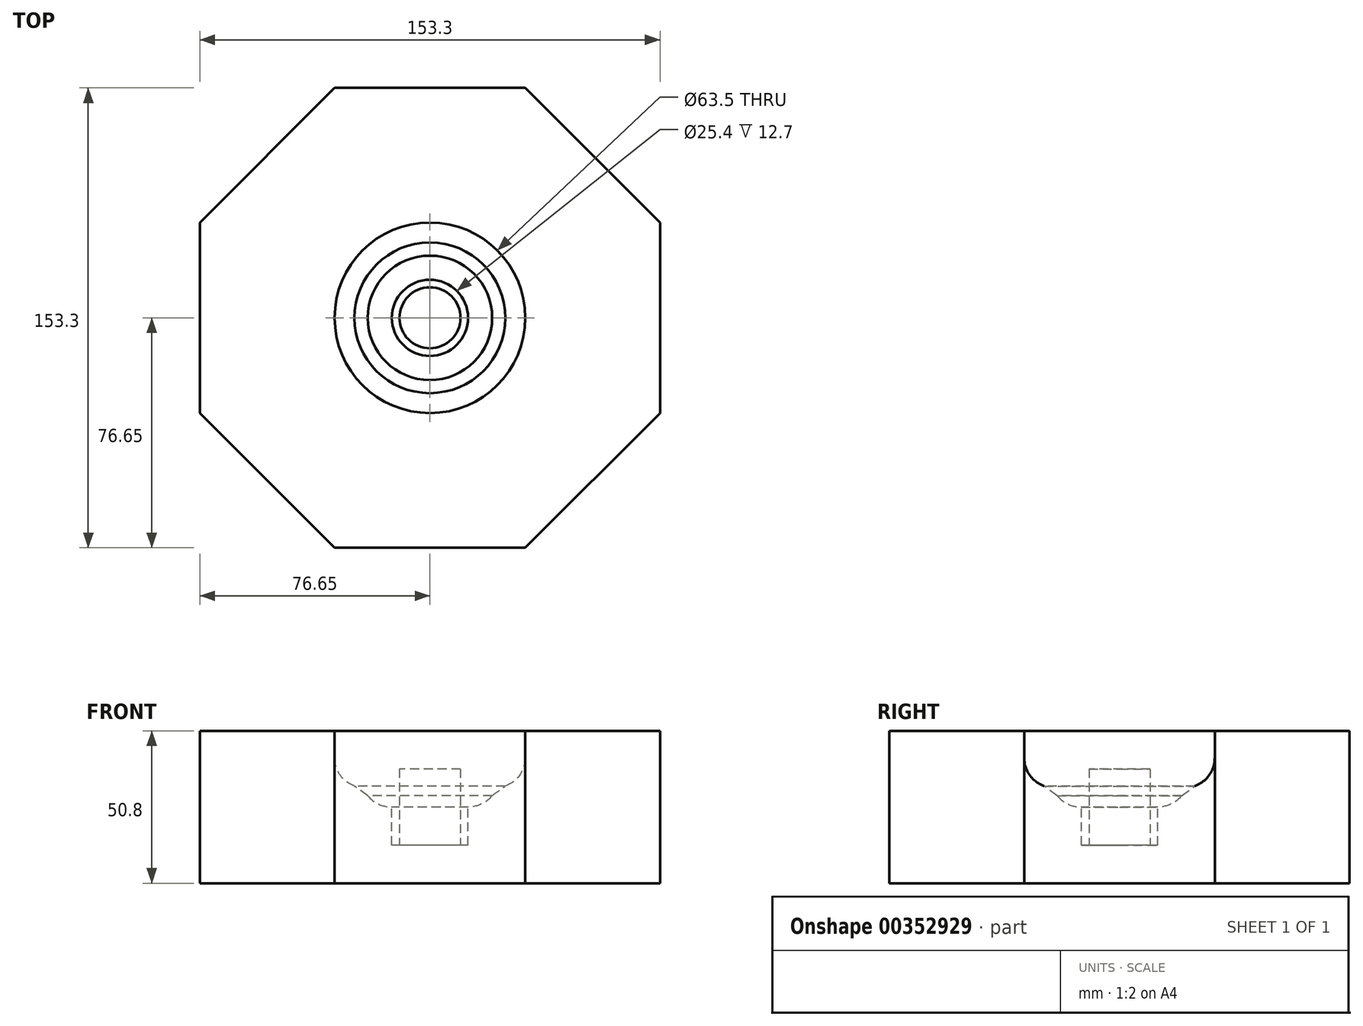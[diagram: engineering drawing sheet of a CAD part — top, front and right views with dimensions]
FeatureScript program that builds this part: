
annotation { "Feature Type Name" : "Feature", "Feature Type Description" : "" }
export const myFeature = defineFeature(function(context is Context, id is Id, definition is map)
    precondition{}
    {
        {
            var Q0;
            Q0=qCreatedBy(makeId("Top.planeOp"),FACE);
            var sketch = newSketch(context, id + "F0", { "sketchPlane" : qUnion([Q0])});
            skCircle(sketch, "E0.cCircle", {"center": v(0, 0) * mm, "radius": 76.65 * mm, "construction": true});
            skLineSegment(sketch, "E0.0", {"start": v(76.65, 31.75) * mm, "end": v(76.65, -31.75) * mm});
            skLineSegment(sketch, "E0.1", {"start": v(76.65, -31.75) * mm, "end": v(31.75, -76.65) * mm});
            skLineSegment(sketch, "E0.2", {"start": v(31.75, -76.65) * mm, "end": v(-31.75, -76.65) * mm});
            skLineSegment(sketch, "E0.3", {"start": v(-31.75, -76.65) * mm, "end": v(-76.65, -31.75) * mm});
            skLineSegment(sketch, "E0.4", {"start": v(-76.65, -31.75) * mm, "end": v(-76.65, 31.75) * mm});
            skLineSegment(sketch, "E0.5", {"start": v(-76.65, 31.75) * mm, "end": v(-31.75, 76.65) * mm});
            skLineSegment(sketch, "E0.6", {"start": v(-31.75, 76.65) * mm, "end": v(31.75, 76.65) * mm});
            skLineSegment(sketch, "E0.7", {"start": v(31.75, 76.65) * mm, "end": v(76.65, 31.75) * mm});
            skPoint(sketch, "E0.0.midPoint", {"position": v(76.65, 0) * mm});
            skSolve(sketch);
        }
        {
            var Q0;
            Q0 = qSketchRegion(id + "F0", true);
            extrude(context, id + "F1", {"entities" : qUnion([Q0]), "depth" : 50.8 * mm});
        }
        {
            var Q0;
            Q0=makeQuery(id+"F1.opExtrude","CAP_FACE",FACE,{"disambiguationData":[OSD([sQuery(id+"F0.wireOp",EDGE,"E0.0"),sQuery(id+"F0.wireOp",EDGE,"E0.1"),sQuery(id+"F0.wireOp",EDGE,"E0.2"),sQuery(id+"F0.wireOp",EDGE,"E0.3"),sQuery(id+"F0.wireOp",EDGE,"E0.4"),sQuery(id+"F0.wireOp",EDGE,"E0.5"),sQuery(id+"F0.wireOp",EDGE,"E0.6"),sQuery(id+"F0.wireOp",EDGE,"E0.7")])],"isStart":false});
            var sketch = newSketch(context, id + "F2", { "sketchPlane" : qUnion([Q0])});
            skCircle(sketch, "E1", {"center": v(0, 0) * mm, "radius": 31.75 * mm});
            skSolve(sketch);
        }
        {
            var Q0;
            Q0 = qSketchRegion(id + "F2", true);
            extrude(context, id + "F3", {"entities" : qUnion([Q0]), "operationType" : NewBodyOperationType.REMOVE, "oppositeDirection" : true, "depth" : 19.05 * mm});
        }
        {
            var Q0;
            Q0=makeQuery(id+"F1.opExtrude","CAP_FACE",FACE,{"disambiguationData":[OSD([sQuery(id+"F0.wireOp",EDGE,"E0.0"),sQuery(id+"F0.wireOp",EDGE,"E0.1"),sQuery(id+"F0.wireOp",EDGE,"E0.2"),sQuery(id+"F0.wireOp",EDGE,"E0.3"),sQuery(id+"F0.wireOp",EDGE,"E0.4"),sQuery(id+"F0.wireOp",EDGE,"E0.5"),sQuery(id+"F0.wireOp",EDGE,"E0.6"),sQuery(id+"F0.wireOp",EDGE,"E0.7")])],"isStart":false});
            var sketch = newSketch(context, id + "F4", { "sketchPlane" : qUnion([Q0])});
            skCircle(sketch, "E2", {"center": v(0, 0) * mm, "radius": 12.7 * mm});
            skSolve(sketch);
        }
        {
            var Q0;
            Q0 = qSketchRegion(id + "F4", true);
            extrude(context, id + "F5", {"entities" : qUnion([Q0]), "operationType" : NewBodyOperationType.REMOVE, "oppositeDirection" : true, "depth" : 38.1 * mm});
        }
        {
            var Q0;
            Q0=makeQuery(id+"F1.opExtrude","CAP_FACE",FACE,{"disambiguationData":[OSD([sQuery(id+"F0.wireOp",EDGE,"E0.0"),sQuery(id+"F0.wireOp",EDGE,"E0.1"),sQuery(id+"F0.wireOp",EDGE,"E0.2"),sQuery(id+"F0.wireOp",EDGE,"E0.3"),sQuery(id+"F0.wireOp",EDGE,"E0.4"),sQuery(id+"F0.wireOp",EDGE,"E0.5"),sQuery(id+"F0.wireOp",EDGE,"E0.6"),sQuery(id+"F0.wireOp",EDGE,"E0.7")])],"isStart":false});
            var sketch = newSketch(context, id + "F6", { "sketchPlane" : qUnion([Q0])});
            skCircle(sketch, "E3", {"center": v(0, 0) * mm, "radius": 22.23 * mm});
            skSolve(sketch);
        }
        {
            var Q0;
            Q0 = qSketchRegion(id + "F6", true);
            extrude(context, id + "F7", {"entities" : qUnion([Q0]), "operationType" : NewBodyOperationType.REMOVE, "oppositeDirection" : true, "depth" : 25.4 * mm});
        }
        {
            var Q0;
            Q0=makeQuery(id+"F3.boolean.opBoolean","COPY",EDGE,{"derivedFrom":makeQuery(id+"F3.opExtrude","CAP_EDGE",EDGE,{"disambiguationData":[OSD([sQuery(id+"F2.wireOp",EDGE,"E1")])],"isStart":false})});
            fillet(context, id + "F8", {"entities" : qUnion([Q0]), "radius" : 10.16 * mm, "tangentPropagation" : true, "allowEdgeOverflow" : false});
        }
        {
            var Q0;
            Q0=makeQuery(id+"F7.boolean.opBoolean","COPY",EDGE,{"derivedFrom":makeQuery(id+"F7.opExtrude","CAP_EDGE",EDGE,{"disambiguationData":[OSD([sQuery(id+"F6.wireOp",EDGE,"E3")])],"isStart":false})});
            fillet(context, id + "F9", {"entities" : qUnion([Q0]), "radius" : 10.16 * mm, "tangentPropagation" : true, "allowEdgeOverflow" : false});
        }
        {
            var Q0;
            Q0=makeQuery(id+"F9.opFillet","BLEND_EDGE",EDGE,{"blendedFrom":[makeQuery(id+"F7.boolean.opBoolean","COPY",EDGE,{"derivedFrom":makeQuery(id+"F7.opExtrude","CAP_EDGE",EDGE,{"disambiguationData":[OSD([sQuery(id+"F6.wireOp",EDGE,"E3")])],"isStart":false})}),makeQuery(id+"F8.opFillet","BLEND_FACE",FACE,{"disambiguationData":[OSD([sQuery(id+"F2.wireOp",EDGE,"E1")])]})],"blendedInto":[makeQuery(id+"F8.opFillet","BLEND_FACE",FACE,{"disambiguationData":[OSD([sQuery(id+"F2.wireOp",EDGE,"E1")])]})]});
            chamfer(context, id + "F10", {"entities" : qUnion([Q0]), "width" : 10.16 * mm, "tangentPropagation" : true});
        }
        {
            var Q0;
            Q0=makeQuery(id+"F5.boolean.opBoolean","COPY",FACE,{"derivedFrom":makeQuery(id+"F5.opExtrude","CAP_FACE",FACE,{"disambiguationData":[OSD([sQuery(id+"F4.wireOp",EDGE,"E2")])],"isStart":false})});
            var sketch = newSketch(context, id + "F11", { "sketchPlane" : qUnion([Q0])});
            skCircle(sketch, "E4", {"center": v(0, 0) * mm, "radius": 10.16 * mm});
            skSolve(sketch);
        }
        {
            var Q0;
            Q0 = qSketchRegion(id + "F11", true);
            extrude(context, id + "F12", {"entities" : qUnion([Q0]), "operationType" : NewBodyOperationType.ADD, "depth" : 25.4 * mm});
        }
    });
